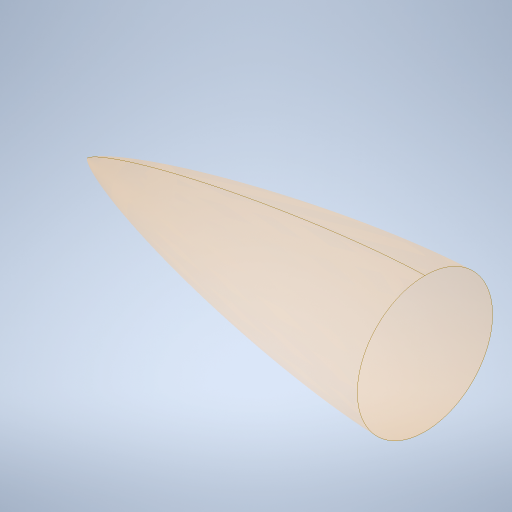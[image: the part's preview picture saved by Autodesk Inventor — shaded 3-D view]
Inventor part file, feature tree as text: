
AUTODESK INVENTOR PART (.ipt)
format: ipt  version: 2024 (Build 280153000, 153)  size: 314,880 bytes
history: native  units: in
note: dims shown in document units (in); Inventor stores cm internally (conversion verified against a paired STEP export)
features: other x2, sketch x1, revolve x1
ambient origin geometry x8: Origin, YZ Plane, XZ Plane, XY Plane, X Axis, Y Axis, Z Axis, Center Point
bodies: Body1 (feature_tree)
feature tree (4):
  sketch  "Sketch1"  dims[d2=0.0in d3=7.5in d5=1.5in d6=90.0deg]
  other  "2D Equation Curve2"
  other  "Ogive Tip"
  revolve  "RevolutionSrf2"  [1 undecoded]
note: 1 required parameter value undecoded (feature->parameter linkage not recoverable at this tier; creation-order binding heuristic only, values carry confidence <= 0.55)
